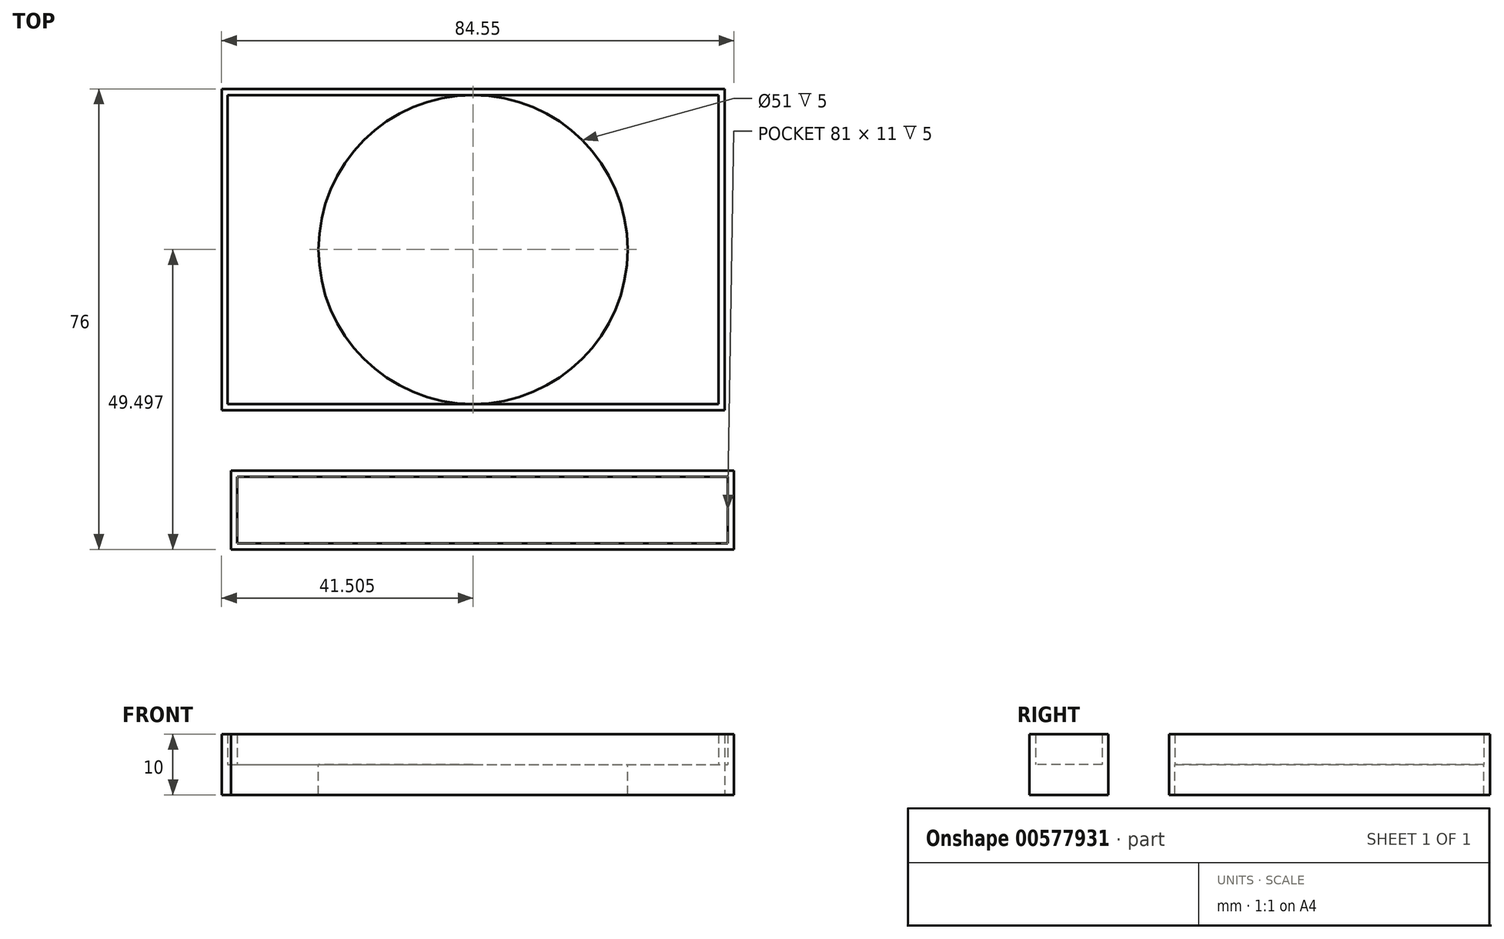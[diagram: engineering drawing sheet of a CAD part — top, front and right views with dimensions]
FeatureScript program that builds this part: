
annotation { "Feature Type Name" : "Feature", "Feature Type Description" : "" }
export const myFeature = defineFeature(function(context is Context, id is Id, definition is map)
    precondition{}
    {
        {
            var Q0;
            Q0=qCreatedBy(makeId("Top.planeOp"),FACE);
            var sketch = newSketch(context, id + "F0", { "sketchPlane" : qUnion([Q0])});
            skLineSegment(sketch, "E0.bottom", {"start": v(-49.58, 22.39) * mm, "end": v(31.42, 22.39) * mm});
            skLineSegment(sketch, "E0.top", {"start": v(-49.58, -28.61) * mm, "end": v(31.42, -28.61) * mm});
            skLineSegment(sketch, "E0.left", {"start": v(-49.58, 22.39) * mm, "end": v(-49.58, -28.61) * mm});
            skLineSegment(sketch, "E0.right", {"start": v(31.42, 22.39) * mm, "end": v(31.42, -28.61) * mm});
            skLineSegment(sketch, "E1.bottom", {"start": v(-50.58, 23.39) * mm, "end": v(32.42, 23.39) * mm});
            skLineSegment(sketch, "E1.top", {"start": v(-50.58, -29.61) * mm, "end": v(32.42, -29.61) * mm});
            skLineSegment(sketch, "E1.left", {"start": v(-50.58, 23.39) * mm, "end": v(-50.58, -29.61) * mm});
            skLineSegment(sketch, "E1.right", {"start": v(32.42, 23.39) * mm, "end": v(32.42, -29.61) * mm});
            skSolve(sketch);
        }
        {
            var Q0;
            Q0=makeQuery(id+"F0.imprint","IMPRINT",FACE,{"disambiguationData":[TD([[makeQuery(id+"F0.imprint","IMPRINT",EDGE,{"derivedFrom":sQuery(id+"F0.wireOp",EDGE,"E0.bottom")}),1.0]])]});
            extrude(context, id + "F1", {"entities" : qUnion([Q0]), "depth" : 10 * mm, "offsetDistance" : 25 * mm});
        }
        {
            var Q0;
            Q0=makeQuery(id+"F0.imprint","IMPRINT",FACE,{"disambiguationData":[TD([[makeQuery(id+"F0.imprint","IMPRINT",EDGE,{"derivedFrom":sQuery(id+"F0.wireOp",EDGE,"E0.bottom")}),-1.0]])]});
            extrude(context, id + "F2", {"entities" : qUnion([Q0]), "operationType" : NewBodyOperationType.ADD, "depth" : 5 * mm, "offsetDistance" : 25 * mm});
        }
        {
            var Q0;
            Q0=qCreatedBy(makeId("Top.planeOp"),FACE);
            var sketch = newSketch(context, id + "F3", { "sketchPlane" : qUnion([Q0])});
            skLineSegment(sketch, "E2.bottom", {"start": v(-49.03, -39.61) * mm, "end": v(33.97, -39.61) * mm});
            skLineSegment(sketch, "E2.top", {"start": v(-49.03, -52.61) * mm, "end": v(33.97, -52.61) * mm});
            skLineSegment(sketch, "E2.left", {"start": v(-49.03, -39.61) * mm, "end": v(-49.03, -52.61) * mm});
            skLineSegment(sketch, "E2.right", {"start": v(33.97, -39.61) * mm, "end": v(33.97, -52.61) * mm});
            skLineSegment(sketch, "E3.bottom", {"start": v(-48.03, -40.61) * mm, "end": v(32.97, -40.61) * mm});
            skLineSegment(sketch, "E3.top", {"start": v(-48.03, -51.61) * mm, "end": v(32.97, -51.61) * mm});
            skLineSegment(sketch, "E3.left", {"start": v(-48.03, -40.61) * mm, "end": v(-48.03, -51.61) * mm});
            skLineSegment(sketch, "E3.right", {"start": v(32.97, -40.61) * mm, "end": v(32.97, -51.61) * mm});
            skSolve(sketch);
        }
        {
            var Q0;
            Q0=makeQuery(id+"F3.imprint","IMPRINT",FACE,{"disambiguationData":[TD([[makeQuery(id+"F3.imprint","IMPRINT",EDGE,{"derivedFrom":sQuery(id+"F3.wireOp",EDGE,"E3.bottom")}),-1.0]])]});
            extrude(context, id + "F4", {"entities" : qUnion([Q0]), "depth" : 5 * mm, "offsetDistance" : 25 * mm});
        }
        {
            var Q0;
            Q0=makeQuery(id+"F3.imprint","IMPRINT",FACE,{"disambiguationData":[TD([[makeQuery(id+"F3.imprint","IMPRINT",EDGE,{"derivedFrom":sQuery(id+"F3.wireOp",EDGE,"E2.bottom")}),-1.0]])]});
            extrude(context, id + "F5", {"entities" : qUnion([Q0]), "operationType" : NewBodyOperationType.ADD, "depth" : 10 * mm, "offsetDistance" : 25 * mm});
        }
        {
            var Q0;
            Q0=makeQuery(id+"F2.opExtrude","CAP_FACE",FACE,{"disambiguationData":[OSD([sQuery(id+"F0.wireOp",EDGE,"E0.bottom"),sQuery(id+"F0.wireOp",EDGE,"E0.top"),sQuery(id+"F0.wireOp",EDGE,"E0.left"),sQuery(id+"F0.wireOp",EDGE,"E0.right")])],"isStart":false});
            var sketch = newSketch(context, id + "F6", { "sketchPlane" : qUnion([Q0])});
            skCircle(sketch, "E4", {"center": v(-9.08, -3.11) * mm, "radius": 25.5 * mm});
            skSolve(sketch);
        }
        {
            var Q0;
            {var subQ0=sQuery(id+"F6.wireOp",EDGE,"E4");var subQ1=makeQuery(id+"F6.imprint","INTERSECT",VERTEX,{"derivedFrom":[makeQuery(id+"F2.opExtrude","CAP_EDGE",EDGE,{"disambiguationData":[OSD([sQuery(id+"F0.wireOp",EDGE,"E0.bottom")])],"isStart":false}),subQ0]});Q0=makeQuery(id+"F6.imprint","IMPRINT",FACE,{"disambiguationData":[TD([[makeQuery(id+"F6.imprint","IMPRINT",EDGE,{"disambiguationData":[TD([[subQ1,-1.0]])],"derivedFrom":subQ0}),1.0]])]});}
            extrude(context, id + "F7", {"entities" : qUnion([Q0]), "operationType" : NewBodyOperationType.REMOVE, "oppositeDirection" : true, "depth" : 25 * mm, "offsetDistance" : 25 * mm});
        }
    });
